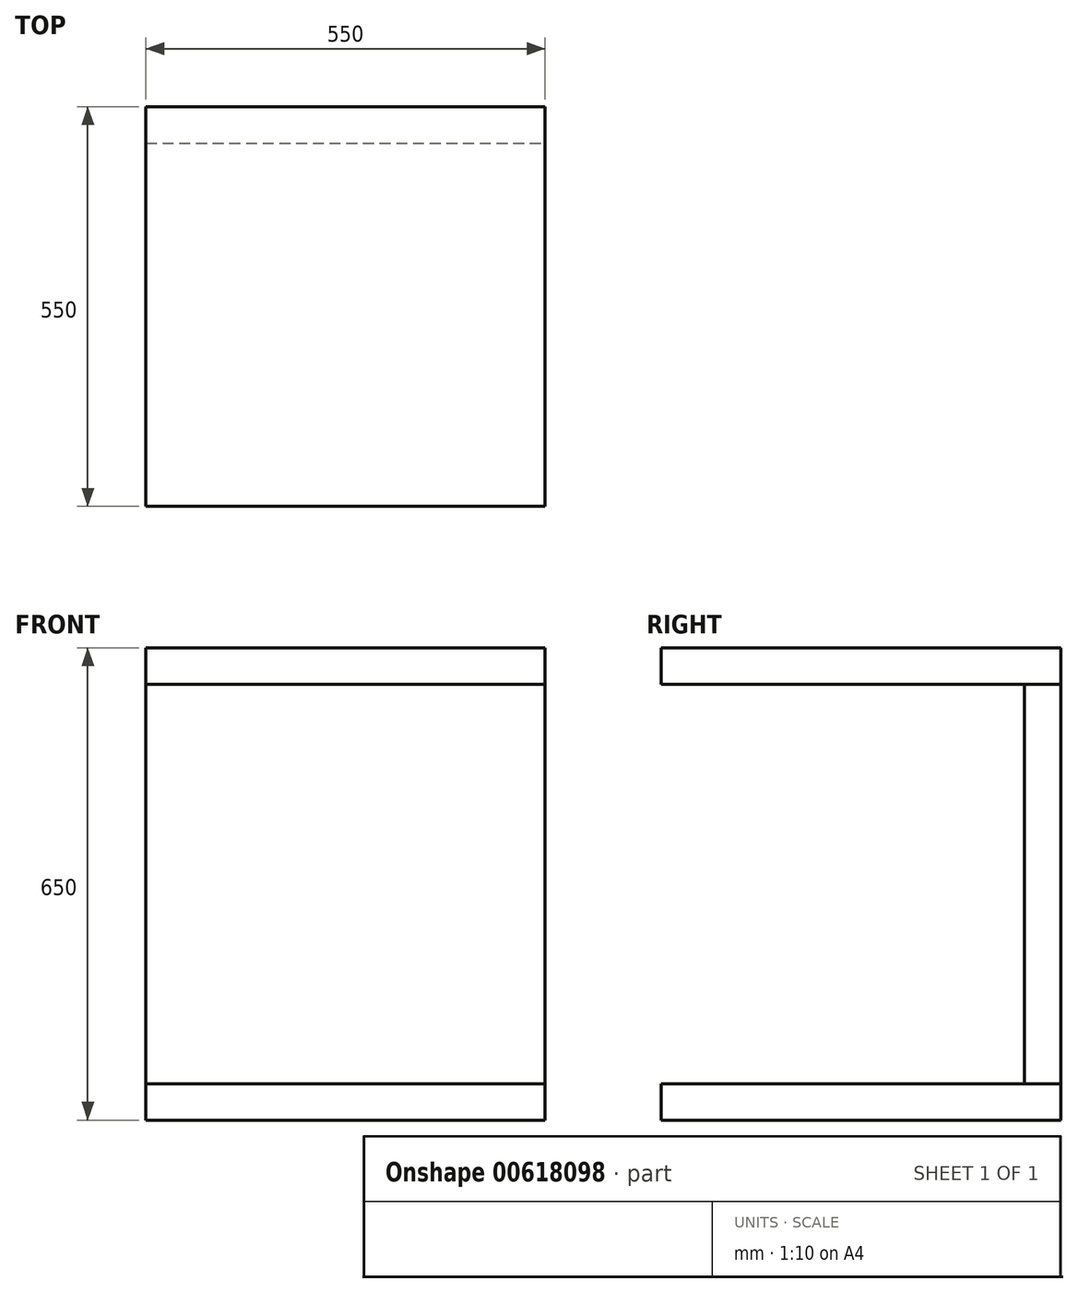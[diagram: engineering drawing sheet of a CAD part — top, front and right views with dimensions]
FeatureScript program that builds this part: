
annotation { "Feature Type Name" : "Feature", "Feature Type Description" : "" }
export const myFeature = defineFeature(function(context is Context, id is Id, definition is map)
    precondition{}
    {
        {
            var Q0;
            Q0=qCreatedBy(makeId("Top.planeOp"),FACE);
            var sketch = newSketch(context, id + "F0", { "sketchPlane" : qUnion([Q0])});
            skLineSegment(sketch, "E0.bottom", {"start": v(-506.65, 513.07) * mm, "end": v(43.35, 513.07) * mm});
            skLineSegment(sketch, "E0.top", {"start": v(-506.65, -36.93) * mm, "end": v(43.35, -36.93) * mm});
            skLineSegment(sketch, "E0.left", {"start": v(-506.65, 513.07) * mm, "end": v(-506.65, -36.93) * mm});
            skLineSegment(sketch, "E0.right", {"start": v(43.35, 513.07) * mm, "end": v(43.35, -36.93) * mm});
            skLineSegment(sketch, "E1", {"start": v(-506.65, 463.07) * mm, "end": v(43.35, 463.07) * mm});
            skSolve(sketch);
        }
        {
            var Q0;
            Q0 = qSketchRegion(id + "F0", true);
            extrude(context, id + "F1", {"entities" : qUnion([Q0]), "depth" : 50 * mm, "offsetDistance" : 25 * mm});
        }
        {
            var Q0;
            Q0=makeQuery(id+"F0.imprint","IMPRINT",FACE,{"disambiguationData":[TD([[makeQuery(id+"F0.imprint","IMPRINT",EDGE,{"derivedFrom":sQuery(id+"F0.wireOp",EDGE,"E0.bottom")}),-1.0]])]});
            extrude(context, id + "F2", {"entities" : qUnion([Q0]), "oppositeDirection" : true, "depth" : 550 * mm, "offsetDistance" : 25 * mm});
        }
        {
            var Q0;
            Q0=makeQuery(id+"F2.opExtrude","CAP_FACE",FACE,{"disambiguationData":[OSD([sQuery(id+"F0.wireOp",EDGE,"E0.bottom"),sQuery(id+"F0.wireOp",EDGE,"E0.left"),sQuery(id+"F0.wireOp",EDGE,"E0.right"),sQuery(id+"F0.wireOp",EDGE,"E1")])],"isStart":false});
            var sketch = newSketch(context, id + "F3", { "sketchPlane" : qUnion([Q0])});
            skPoint(sketch, "E2.0", {"position": v(-506.65, 36.93) * mm});
            skPoint(sketch, "E2.1", {"position": v(43.35, -513.07) * mm});
            skLineSegment(sketch, "E3.bottom", {"start": v(-506.65, 36.93) * mm, "end": v(43.35, 36.93) * mm});
            skLineSegment(sketch, "E3.top", {"start": v(-506.65, -513.07) * mm, "end": v(43.35, -513.07) * mm});
            skLineSegment(sketch, "E3.left", {"start": v(-506.65, 36.93) * mm, "end": v(-506.65, -513.07) * mm});
            skLineSegment(sketch, "E3.right", {"start": v(43.35, 36.93) * mm, "end": v(43.35, -513.07) * mm});
            skSolve(sketch);
        }
        {
            var Q0;
            {var subQ0=sQuery(id+"F3.wireOp",EDGE,"E3.bottom");Q0=makeQuery(id+"F3.imprint","IMPRINT",FACE,{"disambiguationData":[TD([[makeQuery(id+"F3.imprint","IMPRINT",EDGE,{"derivedFrom":subQ0}),-1.0]])]});}
            var Q1;
            {var subQ0=sQuery(id+"F3.wireOp",EDGE,"E3.top");Q1=makeQuery(id+"F3.imprint","IMPRINT",FACE,{"disambiguationData":[TD([[makeQuery(id+"F3.imprint","IMPRINT",EDGE,{"derivedFrom":subQ0}),1.0]])]});}
            extrude(context, id + "F4", {"entities" : qUnion([Q0, Q1]), "depth" : 50 * mm, "offsetDistance" : 25 * mm});
        }
    });
